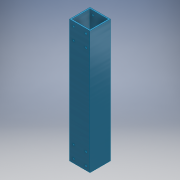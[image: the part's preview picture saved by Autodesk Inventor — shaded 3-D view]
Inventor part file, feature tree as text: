
AUTODESK INVENTOR PART (.ipt)
format: ipt  version: 2018 (Build 220112000, 112)  size: 144,384 bytes
history: native  units: mm
features: extrude x2, sketch x2, other x1
ambient origin geometry x8: Origin, YZ Plane, XZ Plane, XY Plane, X Axis, Y Axis, Z Axis, Center Point
bodies: Body1 (feature_tree)
feature tree (5):
  other  "ソリッド1"
  extrude  "押し出し1"  Depth=50.0mm
  extrude  "押し出し2"  Depth=50.0mm
  sketch  "スケッチ1"
  sketch  "スケッチ2"
